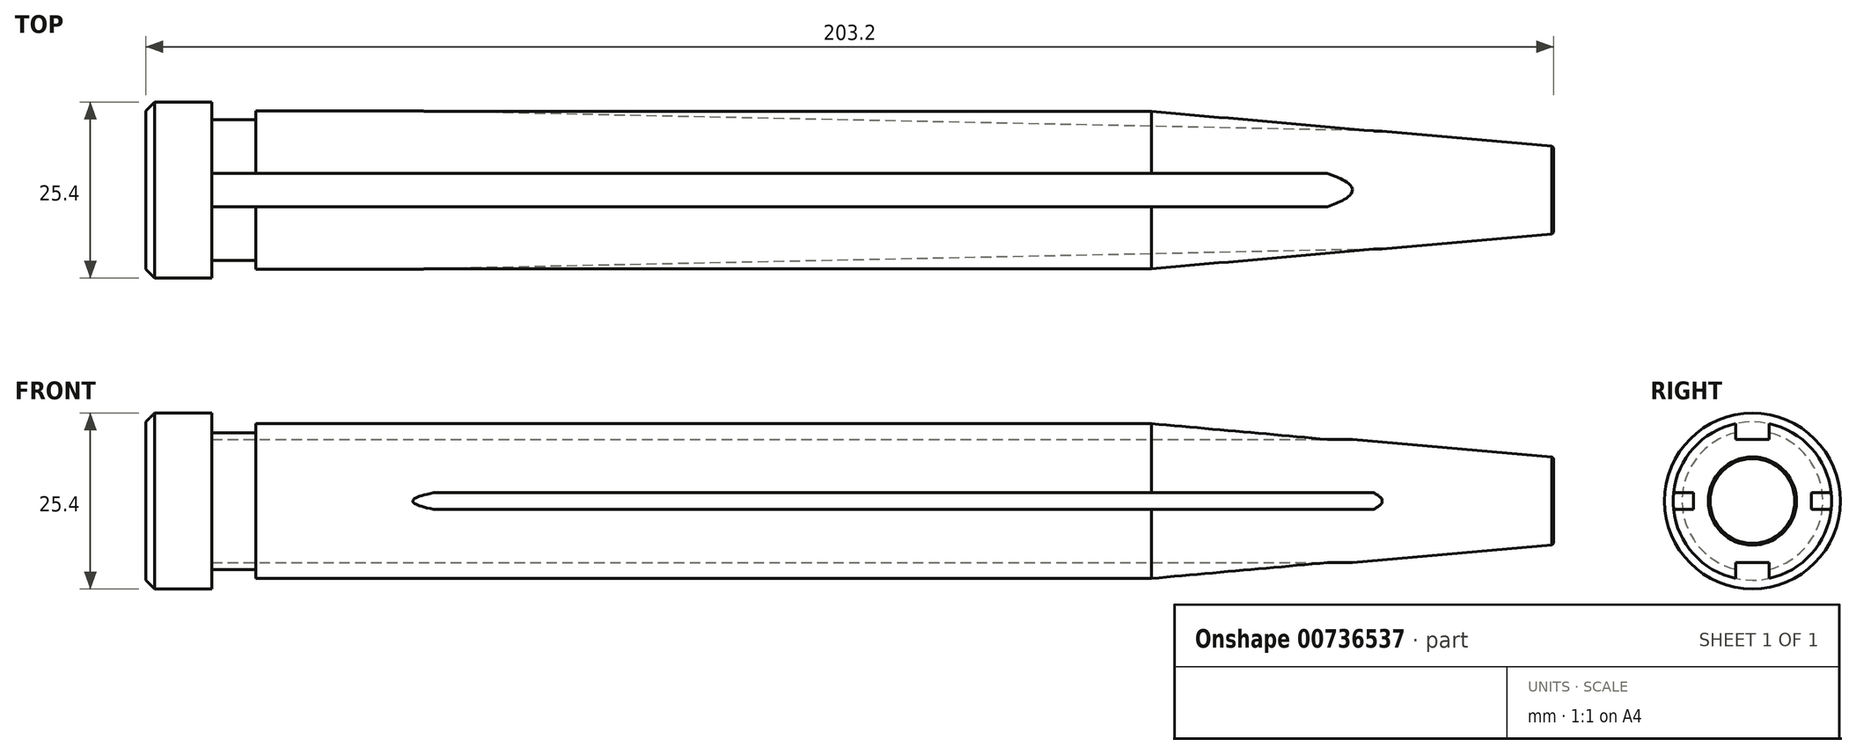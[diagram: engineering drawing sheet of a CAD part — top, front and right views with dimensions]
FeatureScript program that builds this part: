
annotation { "Feature Type Name" : "Feature", "Feature Type Description" : "" }
export const myFeature = defineFeature(function(context is Context, id is Id, definition is map)
    precondition{}
    {
        {
            var Q0;
            Q0=qCreatedBy(makeId("Front.planeOp"),FACE);
            var sketch = newSketch(context, id + "F0", { "sketchPlane" : qUnion([Q0])});
            skLineSegment(sketch, "E0.bottom", {"start": v(0, 0) * mm, "end": v(203.2, 0) * mm});
            skLineSegment(sketch, "E0.top", {"start": v(0, 12.7) * mm, "end": v(9.52, 12.7) * mm});
            skLineSegment(sketch, "E0.left", {"start": v(0, 0) * mm, "end": v(0, 12.7) * mm});
            skLineSegment(sketch, "E1.top", {"start": v(9.52, 10.16) * mm, "end": v(15.88, 10.16) * mm});
            skLineSegment(sketch, "E1.left", {"start": v(9.52, 12.7) * mm, "end": v(9.52, 10.16) * mm});
            skLineSegment(sketch, "E1.right", {"start": v(15.88, 11.43) * mm, "end": v(15.88, 10.16) * mm});
            skLineSegment(sketch, "E2.top", {"start": v(15.88, 11.43) * mm, "end": v(145.14, 11.43) * mm});
            skLineSegment(sketch, "E3", {"start": v(203.2, 0) * mm, "end": v(203.2, 6.35) * mm});
            skLineSegment(sketch, "E4", {"start": v(203.2, 6.35) * mm, "end": v(145.14, 11.43) * mm});
            skSolve(sketch);
        }
        {
            var Q0;
            Q0=qCreatedBy(makeId("Front.planeOp"),FACE);
            var sketch = newSketch(context, id + "F1", { "sketchPlane" : qUnion([Q0])});
            skLineSegment(sketch, "E5", {"start": v(-22.98, 0) * mm, "end": v(118.93, 0) * mm, "construction": true});
            skSolve(sketch);
        }
        {
            var Q0;
            Q0 = qSketchRegion(id + "F0", true);
            var Q1;
            Q1=sQuery(id+"F1.wireOp",EDGE,"E5");
            revolve(context, id + "F2", {"surfaceOperationType" : NewSurfaceOperationType.NEW, "entities" : qUnion([Q0]), "axis" : qUnion([Q1]), "revolveType" : RevolveType.FULL});
        }
        {
            var Q0;
            Q0=makeQuery(id+"F2.opRevolve","SWEPT_EDGE",EDGE,{"disambiguationData":[OSD([sQuery(id+"F0.wireOp",EDGE,"E0.top"),sQuery(id+"F0.wireOp",EDGE,"E0.left")])]});
            chamfer(context, id + "F3", {"entities" : qUnion([Q0]), "width" : 1.27 * mm, "tangentPropagation" : true});
        }
        {
            var Q0;
            Q0=makeQuery(id+"F2.opRevolve","SWEPT_EDGE",EDGE,{"disambiguationData":[OSD([sQuery(id+"F0.wireOp",EDGE,"E3"),sQuery(id+"F0.wireOp",EDGE,"E4")])]});
            chamfer(context, id + "F4", {"entities" : qUnion([Q0]), "width" : 0.25 * mm, "tangentPropagation" : true});
        }
        {
            var Q0;
            Q0=makeQuery(id+"F2.opRevolve","SWEPT_FACE",FACE,{"disambiguationData":[OSD([sQuery(id+"F0.wireOp",EDGE,"E3")])]});
            var sketch = newSketch(context, id + "F5", { "sketchPlane" : qUnion([Q0])});
            skLineSegment(sketch, "E6.bottom", {"start": v(-2.39, 11.43) * mm, "end": v(2.39, 11.43) * mm});
            skLineSegment(sketch, "E6.top", {"start": v(-2.39, 8.9) * mm, "end": v(2.39, 8.9) * mm});
            skLineSegment(sketch, "E6.left", {"start": v(-2.39, 11.43) * mm, "end": v(-2.39, 8.9) * mm});
            skLineSegment(sketch, "E6.right", {"start": v(2.39, 11.43) * mm, "end": v(2.39, 8.9) * mm});
            skPoint(sketch, "E6.middle", {"position": v(0, 10.16) * mm});
            skLineSegment(sketch, "E7.2.0", {"start": v(2.39, -11.43) * mm, "end": v(-2.39, -11.43) * mm});
            skLineSegment(sketch, "E7.2.1", {"start": v(-2.39, -11.43) * mm, "end": v(-2.39, -8.9) * mm});
            skLineSegment(sketch, "E7.2.2", {"start": v(2.39, -8.9) * mm, "end": v(-2.39, -8.9) * mm});
            skLineSegment(sketch, "E7.2.3", {"start": v(2.39, -11.43) * mm, "end": v(2.39, -8.9) * mm});
            skPoint(sketch, "E7.center", {"position": v(0.07, 0.07) * mm});
            skSolve(sketch);
        }
        {
            var Q0;
            Q0=makeQuery(id+"F5.imprint","IMPRINT",FACE,{"disambiguationData":[TD([[makeQuery(id+"F5.imprint","IMPRINT",EDGE,{"derivedFrom":sQuery(id+"F5.wireOp",EDGE,"E6.bottom")}),-1.0]])]});
            var Q1;
            Q1=makeQuery(id+"F5.imprint","IMPRINT",FACE,{"disambiguationData":[TD([[makeQuery(id+"F5.imprint","IMPRINT",EDGE,{"derivedFrom":sQuery(id+"F5.wireOp",EDGE,"E7.2.0")}),-1.0]])]});
            var Q2;
            Q2=makeQuery(id+"F2.opRevolve","SWEPT_FACE",FACE,{"disambiguationData":[OSD([sQuery(id+"F0.wireOp",EDGE,"E1.left")])]});
            extrude(context, id + "F6", {"entities" : qUnion([Q0, Q1]), "operationType" : NewBodyOperationType.REMOVE, "endBound" : BoundingType.UP_TO_SURFACE, "oppositeDirection" : true, "depth" : 25.4 * mm, "endBoundEntityFace" : qUnion([Q2]), "offsetDistance" : 25.4 * mm});
        }
        {
            var Q0;
            Q0=qCreatedBy(makeId("Top.planeOp"),FACE);
            var sketch = newSketch(context, id + "F7", { "sketchPlane" : qUnion([Q0])});
            skLineSegment(sketch, "E8", {"start": v(180.94, 8.46) * mm, "end": v(28.57, 11.64) * mm});
            skLineSegment(sketch, "E9", {"start": v(28.58, 11.64) * mm, "end": v(180.94, 11.64) * mm});
            skLineSegment(sketch, "E10", {"start": v(180.94, 8.46) * mm, "end": v(180.94, 11.64) * mm});
            skLineSegment(sketch, "E11.MirrorCS", {"start": v(28.58, -11.64) * mm, "end": v(180.94, -11.64) * mm});
            skLineSegment(sketch, "E12.MirrorCS", {"start": v(180.94, -8.46) * mm, "end": v(28.57, -11.64) * mm});
            skLineSegment(sketch, "E13.MirrorCS", {"start": v(180.94, -11.64) * mm, "end": v(180.94, -8.46) * mm});
            skSolve(sketch);
        }
        {
            var Q0;
            Q0 = qSketchRegion(id + "F7", true);
            extrude(context, id + "F8", {"entities" : qUnion([Q0]), "operationType" : NewBodyOperationType.REMOVE, "endBound" : BoundingType.SYMMETRIC, "depth" : 2.4 * mm, "offsetDistance" : 25.4 * mm});
        }
    });
